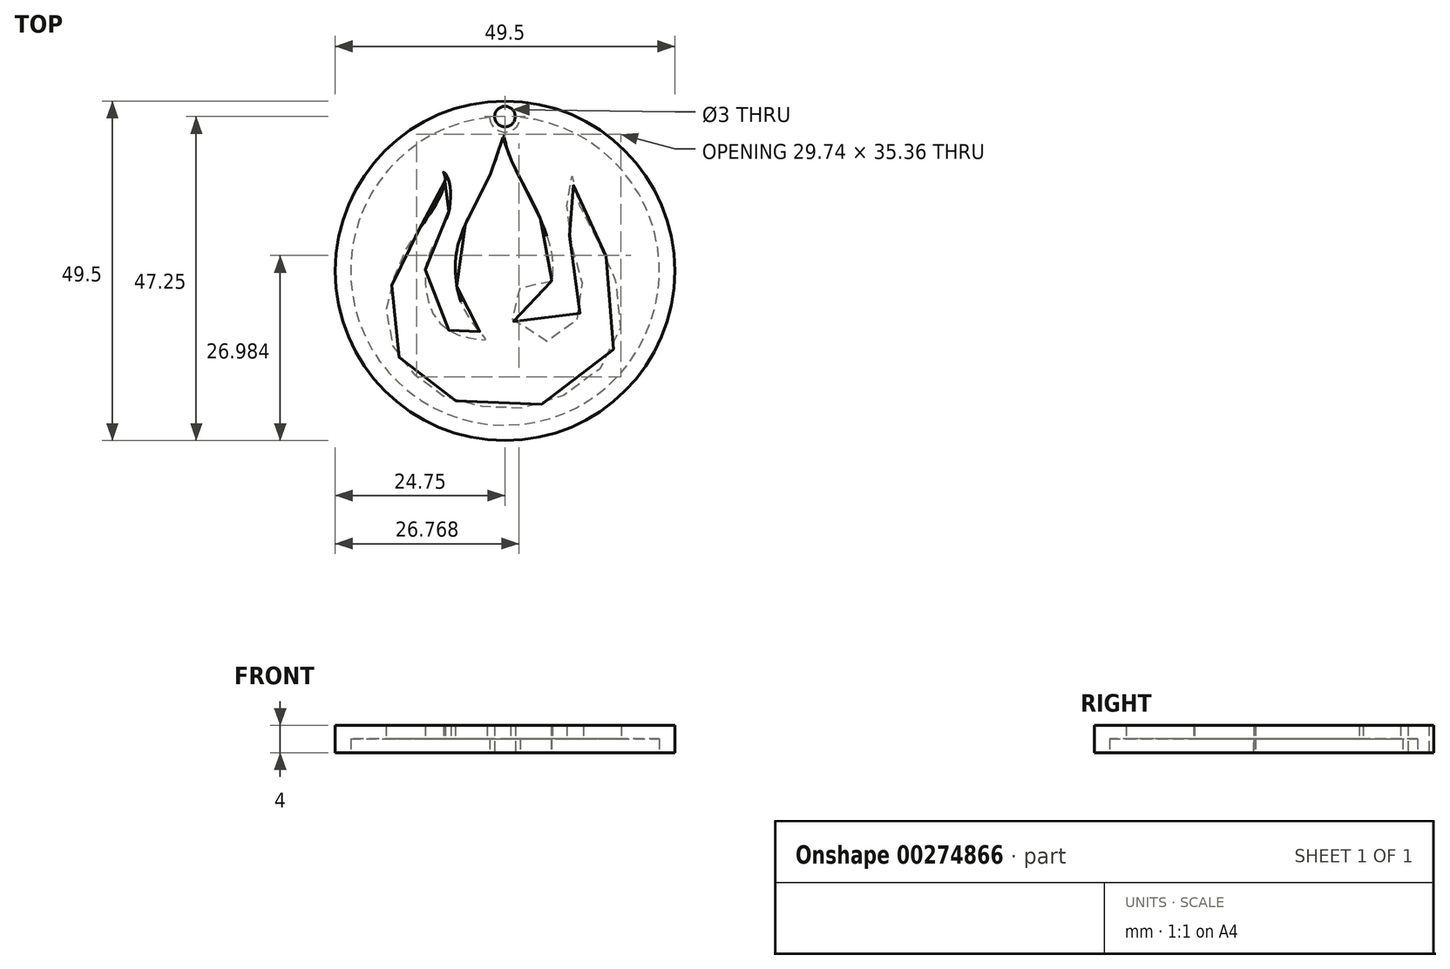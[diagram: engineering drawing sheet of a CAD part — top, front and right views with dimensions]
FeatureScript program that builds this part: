
annotation { "Feature Type Name" : "Feature", "Feature Type Description" : "" }
export const myFeature = defineFeature(function(context is Context, id is Id, definition is map)
    precondition{}
    {
        {
            var Q0;
            Q0=qCreatedBy(makeId("Top.planeOp"),FACE);
            var sketch = newSketch(context, id + "F0", { "sketchPlane" : qUnion([Q0])});
            skCircle(sketch, "E0", {"center": v(0, 0) * mm, "radius": 24.75 * mm});
            skArc(sketch, "E1", {"start": v(-2.25, 22.39) * mm, "mid": v(0, -22.5) * mm, "end": v(2.25, 22.39) * mm});
            skFitSpline(sketch, "E2", {"points": [v(7.05, -1.6) * mm, v(4.97, -1.26) * mm, v(3.12, -1.64) * mm, v(1.57, -3.34) * mm, v(0.95, -4.55) * mm, v(0.98, -6.72) * mm, v(2.96, -9.4) * mm, v(6.37, -10.2) * mm, v(9.05, -8.85) * mm, v(10.52, -7.14) * mm, v(11.3, -4.47) * mm, v(11.37, -2.34) * mm, v(10.83, 0) * mm, v(10.12, 2.3) * mm, v(9.27, 5.87) * mm, v(9.01, 8.48) * mm, v(9.22, 11.1) * mm, v(9.6, 13.16) * mm, v(9.76, 13.88) * mm, v(10, 12.44) * mm, v(10.33, 10.99) * mm, v(10.91, 9.43) * mm, v(12.33, 6.5) * mm, v(13.9, 3.72) * mm, v(15.3, 0.94) * mm, v(16.33, -2.2) * mm, v(16.98, -6.41) * mm, v(16.2, -10.6) * mm, v(14.2, -13.86) * mm, v(11.97, -15.95) * mm, v(8.4, -18.22) * mm, v(5.36, -19.46) * mm, v(2.15, -20.04) * mm, v(-0.41, -20.1) * mm, v(-3.8, -19.73) * mm, v(-7.02, -19.02) * mm, v(-9.07, -18.22) * mm, v(-11.27, -16.81) * mm, v(-12.84, -15.46) * mm, v(-13.9, -14.4) * mm, v(-15.58, -12.33) * mm, v(-16.87, -9.41) * mm, v(-17.3, -7.03) * mm, v(-17.2, -4.97) * mm, v(-17.03, -3.92) * mm, v(-16.26, -1.23) * mm, v(-15.51, 0.84) * mm, v(-14.92, 2.15) * mm, v(-14.32, 3.27) * mm, v(-13.65, 4.35) * mm, v(-12.95, 5.36) * mm, v(-12.15, 6.55) * mm, v(-11.37, 7.7) * mm, v(-10.42, 9.16) * mm, v(-9.69, 10.37) * mm, v(-9.2, 11.41) * mm, v(-8.86, 12.47) * mm, v(-8.73, 13.17) * mm, v(-8.73, 13.7) * mm, v(-8.96, 14.45) * mm, v(-8.42, 13.77) * mm, v(-8.1, 12.78) * mm, v(-7.91, 11.6) * mm, v(-7.97, 10.06) * mm, v(-8.24, 8.48) * mm, v(-8.79, 6.87) * mm, v(-9.26, 5.8) * mm, v(-10.2, 4.3) * mm, v(-10.9, 2.81) * mm, v(-11.49, 0.98) * mm, v(-11.63, -0.73) * mm, v(-11.54, -2.34) * mm, v(-11.29, -4.17) * mm, v(-10.52, -6.15) * mm, v(-9.21, -7.88) * mm, v(-7.47, -9.05) * mm, v(-5.7, -9.65) * mm, v(-4.34, -9.9) * mm, v(-3.13, -10.04) * mm, v(-2.58, -10.09) * mm, v(-2.8, -9.88) * mm, v(-3.2, -9.4) * mm, v(-3.67, -8.82) * mm, v(-4.18, -8.2) * mm, v(-4.68, -7.54) * mm, v(-5.21, -6.78) * mm, v(-5.87, -5.7) * mm, v(-6.36, -4.72) * mm, v(-6.8, -3.31) * mm, v(-7.06, -2.05) * mm, v(-7.22, -0.19) * mm, v(-7.24, 1.35) * mm, v(-7, 3.1) * mm, v(-6.63, 4.47) * mm, v(-6.02, 6.2) * mm, v(-5.41, 7.57) * mm, v(-4.8, 8.9) * mm, v(-3.79, 10.86) * mm, v(-3.34, 11.8) * mm, v(-2.88, 12.66) * mm, v(-2.34, 13.68) * mm, v(-1.98, 14.42) * mm, v(-1.63, 15.16) * mm, v(-1.3, 15.92) * mm, v(-1.08, 16.6) * mm, v(-0.86, 17.26) * mm, v(-0.71, 17.76) * mm, v(-0.59, 18.27) * mm, v(-0.47, 18.72) * mm, v(-0.38, 19.1) * mm, v(-0.3, 19.38) * mm, v(-0.23, 19.72) * mm, v(-0.18, 19.93) * mm, v(-0.1, 19.5) * mm, v(0.12, 18.54) * mm, v(0.22, 18.07) * mm, v(0.31, 17.72) * mm, v(0.43, 17.37) * mm, v(0.54, 17.04) * mm, v(0.77, 16.49) * mm, v(0.94, 16.13) * mm, v(1.13, 15.67) * mm, v(1.5, 14.87) * mm, v(1.9, 14.1) * mm, v(2.5, 12.97) * mm, v(3.12, 11.8) * mm, v(4.37, 9.3) * mm, v(5.27, 7.3) * mm, v(6.07, 5.18) * mm, v(6.6, 3.33) * mm, v(6.88, 1.81) * mm, v(6.94, 0) * mm, v(6.87, -0.92) * mm, v(6.8, -1.4) * mm, v(6.76, -1.5) * mm, v(6.42, -1.44) * mm], "startDerivative": vector(-216.33, 57.03) * mm, "endDerivative": vector(-8.5, -6.23) * mm});
            skLineSegment(sketch, "E3", {"start": v(6.73, -1.52) * mm, "end": v(6.81, -1.25) * mm});
            skArc(sketch, "E4", {"start": v(-2.25, 22.39) * mm, "mid": v(0, 20.25) * mm, "end": v(2.25, 22.39) * mm});
            skCircle(sketch, "E5.0", {"center": v(0, 22.5) * mm, "radius": 1.5 * mm});
            skSolve(sketch);
        }
        {
            var Q0;
            Q0=makeQuery(id+"F0.imprint","IMPRINT",FACE,{"disambiguationData":[TD([[makeQuery(id+"F0.imprint","IMPRINT",EDGE,{"derivedFrom":sQuery(id+"F0.wireOp",EDGE,"E1")}),1.0]])]});
            var Q1;
            Q1=makeQuery(id+"F0.imprint","IMPRINT",FACE,{"disambiguationData":[TD([[makeQuery(id+"F0.imprint","IMPRINT",EDGE,{"derivedFrom":sQuery(id+"F0.wireOp",EDGE,"E0")}),1.0]])]});
            var Q2;
            Q2=makeQuery(id+"F0.imprint","IMPRINT",FACE,{"disambiguationData":[TD([[makeQuery(id+"F0.imprint","IMPRINT",EDGE,{"derivedFrom":sQuery(id+"F0.wireOp",EDGE,"E2")}),-1.0]])]});
            extrude(context, id + "F1", {"entities" : qUnion([Q0, Q1, Q2]), "depth" : 4 * mm});
        }
        {
            var Q0;
            Q0=makeQuery(id+"F0.imprint","IMPRINT",FACE,{"disambiguationData":[TD([[makeQuery(id+"F0.imprint","IMPRINT",EDGE,{"derivedFrom":sQuery(id+"F0.wireOp",EDGE,"E1")}),1.0]])]});
            extrude(context, id + "F2", {"entities" : qUnion([Q0]), "operationType" : NewBodyOperationType.REMOVE, "depth" : 2 * mm});
        }
    });
